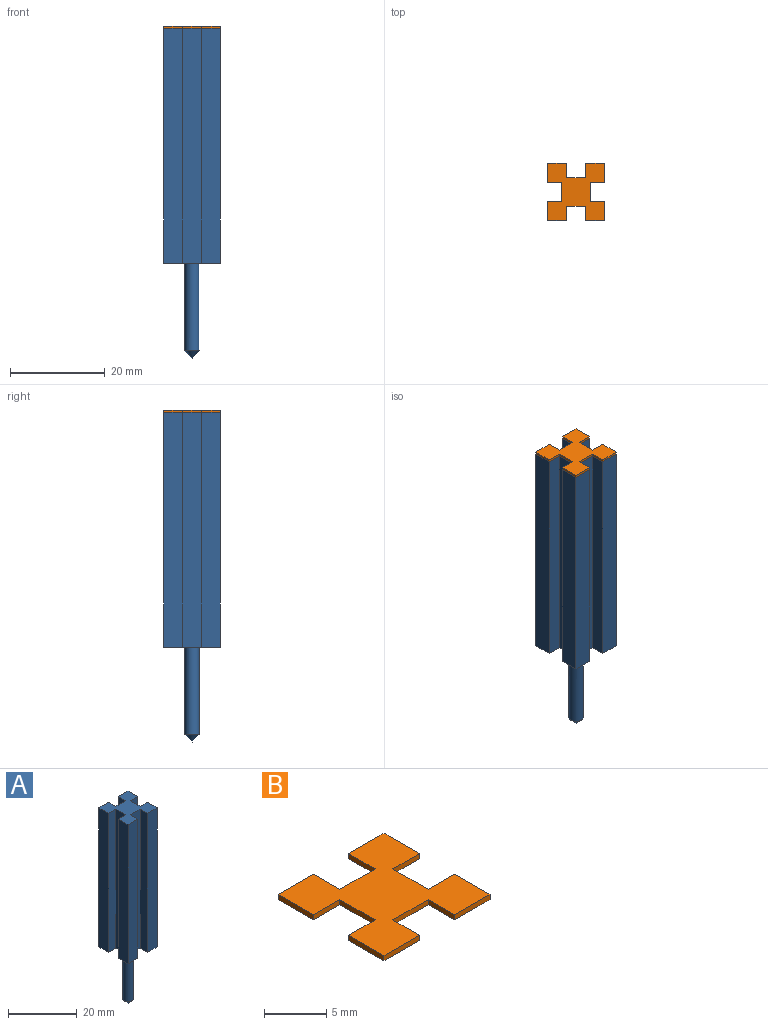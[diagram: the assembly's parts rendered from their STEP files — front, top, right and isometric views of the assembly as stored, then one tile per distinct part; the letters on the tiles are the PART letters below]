
ASSEMBLY  parts=2 mates=1
PART A: 24 faces, bbox 12x12x69.5 mm
  f0: plane 49.5x4mm, normal (0,-1,0), area 198mm2, adj f1,f8,f20,f21
  f1: plane 49.5x4mm, normal (1,0,0), area 198mm2, adj f0,f9,f20,f21
  f2: plane 49.5x4mm, normal (1,0,0), area 198mm2, adj f3,f11,f20,f21
  f3: plane 49.5x4mm, normal (0,1,0), area 198mm2, adj f2,f12,f20,f21
  f4: plane 49.5x4mm, normal (0,1,0), area 198mm2, adj f5,f14,f20,f21
  f5: plane 49.5x4mm, normal (-1,0,0), area 198mm2, adj f4,f15,f20,f21
  f6: plane 49.5x4mm, normal (-1,0,0), area 198mm2, adj f7,f17,f20,f21
  f7: plane 49.5x4mm, normal (0,-1,0), area 198mm2, adj f6,f18,f20,f21
  f8: plane 49.5x3mm, normal (-1,0,0), area 148.5mm2, adj f0,f19,f20,f21
  f9: plane 49.5x3mm, normal (0,1,0), area 148.5mm2, adj f1,f10,f20,f21
  f10: plane 49.5x4mm, normal (1,0,0), area 198mm2, adj f9,f11,f20,f21
  f11: plane 49.5x3mm, normal (0,-1,0), area 148.5mm2, adj f2,f10,f20,f21
  f12: plane 49.5x3mm, normal (-1,0,0), area 148.5mm2, adj f3,f13,f20,f21
  f13: plane 49.5x4mm, normal (0,1,0), area 198mm2, adj f12,f14,f20,f21
  f14: plane 49.5x3mm, normal (1,0,0), area 148.5mm2, adj f4,f13,f20,f21
  f15: plane 49.5x3mm, normal (0,-1,0), area 148.5mm2, adj f5,f16,f20,f21
  f16: plane 49.5x4mm, normal (-1,0,0), area 198mm2, adj f15,f17,f20,f21
  f17: plane 49.5x3mm, normal (0,1,0), area 148.5mm2, adj f6,f16,f20,f21
  f18: plane 49.5x3mm, normal (1,0,0), area 148.5mm2, adj f7,f19,f20,f21
  f19: plane 49.5x4mm, normal (0,-1,0), area 198mm2, adj f8,f18,f20,f21
  f20: plane 12x12mm, normal (0,0,-1), area 88.9mm2, adj f0,f1,f2,f3,f4,f5,f6,f7
  f21: plane 12x12mm, normal (0,0,1), area 96mm2, adj f0,f1,f2,f3,f4,f5,f6,f7
  f22: cylinder r=1.5mm len=18.5mm, axis (0,0,1), area 174.4mm2, adj f20,f23
  f23: cone r=1.5mm half-angle=45deg, axis (0,0,1), area 10mm2, adj f22
PART B: 22 faces, bbox 12x12x0.5 mm
  f0: plane 4x0.5mm, normal (0,-1,0), area 2mm2, adj f1,f8,f20,f21
  f1: plane 4x0.5mm, normal (1,0,0), area 2mm2, adj f0,f9,f20,f21
  f2: plane 4x0.5mm, normal (1,0,0), area 2mm2, adj f3,f11,f20,f21
  f3: plane 4x0.5mm, normal (0,1,0), area 2mm2, adj f2,f12,f20,f21
  f4: plane 4x0.5mm, normal (0,1,0), area 2mm2, adj f5,f14,f20,f21
  f5: plane 4x0.5mm, normal (-1,0,0), area 2mm2, adj f4,f15,f20,f21
  f6: plane 4x0.5mm, normal (-1,0,0), area 2mm2, adj f7,f17,f20,f21
  f7: plane 4x0.5mm, normal (0,-1,0), area 2mm2, adj f6,f18,f20,f21
  f8: plane 3x0.5mm, normal (-1,0,0), area 1.5mm2, adj f0,f19,f20,f21
  f9: plane 3x0.5mm, normal (0,1,0), area 1.5mm2, adj f1,f10,f20,f21
  f10: plane 4x0.5mm, normal (1,0,0), area 2mm2, adj f9,f11,f20,f21
  f11: plane 3x0.5mm, normal (0,-1,0), area 1.5mm2, adj f2,f10,f20,f21
  f12: plane 3x0.5mm, normal (-1,0,0), area 1.5mm2, adj f3,f13,f20,f21
  f13: plane 4x0.5mm, normal (0,1,0), area 2mm2, adj f12,f14,f20,f21
  f14: plane 3x0.5mm, normal (1,0,0), area 1.5mm2, adj f4,f13,f20,f21
  f15: plane 3x0.5mm, normal (0,-1,0), area 1.5mm2, adj f5,f16,f20,f21
  f16: plane 4x0.5mm, normal (-1,0,0), area 2mm2, adj f15,f17,f20,f21
  f17: plane 3x0.5mm, normal (0,1,0), area 1.5mm2, adj f6,f16,f20,f21
  f18: plane 3x0.5mm, normal (1,0,0), area 1.5mm2, adj f7,f19,f20,f21
  f19: plane 4x0.5mm, normal (0,-1,0), area 2mm2, adj f8,f18,f20,f21
  f20: plane 12x12mm, normal (0,0,-1), area 96mm2, adj f0,f1,f2,f3,f4,f5,f6,f7
  f21: plane 12x12mm, normal (0,0,1), area 96mm2, adj f0,f1,f2,f3,f4,f5,f6,f7
PLACE A t=(4.06,12.17,-31.2)mm
PLACE B t=(4.06,12.17,18.3)mm
MATE planar A.f22 <-> B.f20  axis (0,0,1) through (10.06,18.17,18.3)mm
